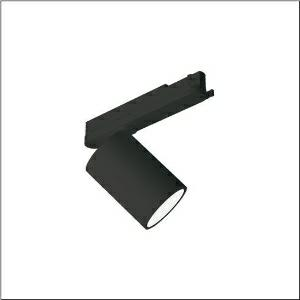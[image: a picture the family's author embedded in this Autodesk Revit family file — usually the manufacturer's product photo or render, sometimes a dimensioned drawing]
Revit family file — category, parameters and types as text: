
# Revit family: spot_31_51sf32mad4b
name_source: partatom
category: Lighting Fixtures
units: mm (PartAtom-declared; Revit-internal decimal feet)

## family parameters
Cut with Voids When Loaded = No
Host = Face
Light Source = No
Part Type = Normal
Room Calculation Point = No
Round Connector Dimension = Use Diameter
Shared = No

## types (1)
- --- (1 x LED, 5140 lm, 41.6 W, 4000K)
    Apparent Load = 42 VA
    CIE Flux Codes = 93 97 99 100 100
    Color Rendering = 90
    Color Temperature = 4000K
    Default Elevation = 1800 mm
    Description = Spot 31, directional spotlight, light control with lens, of PMMA, LED rated luminous flux: 4.930lm, light colour: 940, control gear: ECG Multilumen, with 3-phase adapter, mains connection: 220..240V, AC, 50/60Hz, of aluminium, jet black (RAL 9005), length: 213mm, diameter: 90mm, protection rating (complete): IP20, insulation class (complete): insulation class I (protective earthing), certification: CE, impact resistance: IK02, permissible ambient temperature for indoor applications: -20..+40°C, packaging unit: 1 piece
    Height = 175 mm
    Lamp = 1 x LED
    Lamp Light Flux = 5140 lm
    Lamp Power = 41.6 W
    Lamp count = 1
    Length = 90 mm
    Luminous efficacy = 124 lm/W
    Manufacturer = Siteco
    ModVariant = No
    Model = 51SF32MAD4B
    Mounting Place = Ceiling
    Mounting Type = Pendant
    Number of Poles = 1
    OnlyDefault = Yes
    Power Factor = 1
    Product Name = Spot 31
    Product group = directional spotlight
    ProductGroupID = 906
    Protection Class = Protection class I
    Protection Degree = IP 20
    RLX_Detail_Level = 1
    RLX_Emergency_Light_Flux = 0 lm
    RLX_Emergency_Type = 0
    RLX_Emergency_Type_DB = No
    RlxData = <blob elided: 20901 chars, md5=c1aa4d01>
    Socket = socket
    Standby Power = 0 W
    System Light Flux = 5140 lm
    System Power = 42 W
    Type Comments = factory setting: luminous flux: 100 % | (ON | ON | ON | ON) | 1050 mA
    Type Image = l_1273723.jpg
    URL = http://relux.com
    VarID = @adj_146602
    Voltage = 0 V
    Weight = 0.00 kg
    Width = 0 mm  [stored 0 ft]

note: [stored X ft] marks values corroborated as IEEE doubles in the binary element streams (Revit-internal decimal feet)

## geometry (parser evidence)
native form markers: Blend x4, Sweep x10
no freeform markers — native parametric forms only
